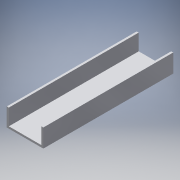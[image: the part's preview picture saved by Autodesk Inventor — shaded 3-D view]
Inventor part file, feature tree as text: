
AUTODESK INVENTOR PART (.ipt)
format: ipt  version: 2016 (Build 200138000, 138)  size: 98,816 bytes
history: native  units: in
note: dims shown in document units (in); Inventor stores cm internally (conversion verified against a paired STEP export)
features: extrude x1, sketch x1
ambient origin geometry x8: Origin, YZ Plane, XZ Plane, XY Plane, X Axis, Y Axis, Z Axis, Center Point
bodies: Solid1 (feature_tree)
feature tree (2):
  extrude  "Extrusion1"  Depth=1.125in
  sketch  "Sketch1"  dims[d0=2.25in d1=1.125in d2=0.125in d3=8.0in d4=0.0in d13=1.125in]
